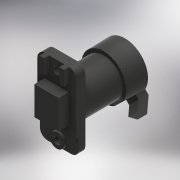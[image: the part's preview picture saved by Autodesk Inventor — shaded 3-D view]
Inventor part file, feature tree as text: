
AUTODESK INVENTOR PART (.ipt)
format: ipt  version: 2017 (Build 210142000, 142)  size: 307,200 bytes
history: native  units: mm
features: sketch x12, extrude x9, projected_geometry x8, other x2, hole x1, fillet x1, revolve x1, chamfer x1, plane x1
ambient origin geometry x8: Origin, YZ Plane, XZ Plane, XY Plane, X Axis, Y Axis, Z Axis, Center Point
bodies: Solid1 (feature_tree)
feature tree (36):
  extrude  "Extrusion1"  Depth=21.0mm
  extrude  "Extrusion2"  Depth=15.9mm
  extrude  "Extrusion3"  Depth=1.25mm
  extrude  "Extrusion4"  Depth=1.25mm
  extrude  "Extrusion5"  Depth=4.2mm
  hole  "Hole1"  [1 undecoded]
  fillet  "Fillet1"  Radius=7.8mm
  extrude  "Extrusion6"  Depth=2.8mm TaperAngle=0.0deg
  revolve  "Revolution1"  [1 undecoded]
  chamfer  "Chamfer1"  Distance=10.3mm
  sketch  "Sketch9"  dims[d22=16.5mm]
  plane  "Work Plane2"
  extrude  "Extrusion7"  Depth=2.1mm
  extrude  "Extrusion8"  Depth=2.1mm
  extrude  "Extrusion9"  TaperAngle=90.0deg  [1 undecoded]
  sketch  "Sketch1"  dims[d0=10.6mm d1=21.0mm]
  sketch  "Sketch2"  dims[d2=1.8mm d3=0.0mm d4=15.9mm]
  projected_geometry  "Projected Loop1"
  sketch  "Sketch3"  dims[d5=0.7mm d6=0.0mm d7=1.25mm]
  projected_geometry  "Projected Loop2"
  sketch  "Sketch4"  dims[d8=4.0mm d9=1.25mm]
  sketch  "Sketch5"  dims[d10=4.0mm d11=4.2mm]
  sketch  "Sketch6"  dims[d12=1.4mm d13=0.0mm d14=6.6mm d15=7.8mm]
  projected_geometry  "Projected Loop3"
  projected_geometry  "Projected Loop4"
  sketch  "Sketch7"  dims[d16=6.0mm d17=2.8mm d18=0.0mm]
  sketch  "Sketch8"  dims[d19=3.9mm d20=2.8mm d21=0.0mm]
  projected_geometry  "Projected Loop5"
  other  "Work Point3"
  other  "Work Axis1"
  sketch  "Sketch11"  dims[d23=2.0mm d24=6.0mm d25=4.0mm d26=2.0mm d27=90.0deg d28=8.0mm d29=20.594885mm]
  projected_geometry  "Projected Loop6"
  sketch  "Sketch12"  dims[d30=2.1mm]
  projected_geometry  "Projected Loop7"
  sketch  "Sketch13"  dims[d31=10.35mm d32=10.3mm d33=0.0mm d34=12.3mm d35=12.58mm d36=90.0deg d37=2.6mm d38=4.6mm d39=0.5mm d40=0.12mm d41=2.0mm d42=45.0deg d43=45.0deg d44=135.0deg d45=3.65mm d46=2.6mm d47=3.3mm d48=0.0mm d49=0.3mm d50=1.0mm d51=0.0mm d52=0.0mm d53=2.6mm d54=2.1mm d55=6.981317mm d56=4.0mm d57=0.3mm d58=0.0mm]
  projected_geometry  "Projected Loop8"
note: 3 required parameter values undecoded (feature->parameter linkage not recoverable at this tier; creation-order binding heuristic only, values carry confidence <= 0.55)